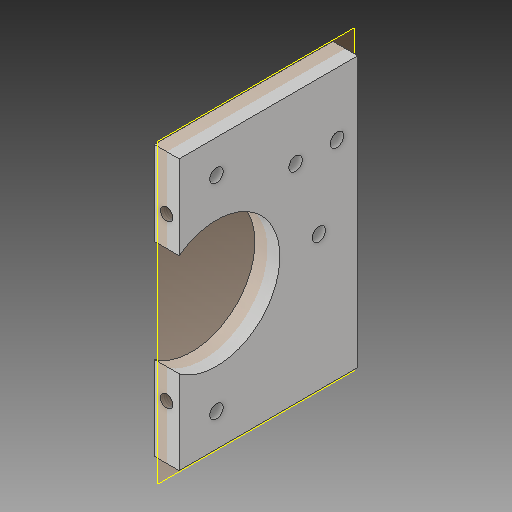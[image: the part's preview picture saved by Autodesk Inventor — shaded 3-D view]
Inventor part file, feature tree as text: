
AUTODESK INVENTOR PART (.ipt)
format: ipt  version: 2018 (Build 220112000, 112)  size: 161,792 bytes
history: native  units: mm
features: extrude x5, sketch x5, thread x4, reference x2, plane x1
ambient origin geometry x8: Origin, YZ Plane, XZ Plane, XY Plane, X Axis, Y Axis, Z Axis, Center Point
bodies: Solid1 (feature_tree)
feature tree (17):
  extrude  "Extrusion1"  Depth=86.0mm
  extrude  "Extrusion2"  Depth=12.0mm
  plane  "Work Plane1"
  extrude  "Extrusion3"  Depth=98.429mm
  extrude  "Extrusion4"  Depth=6.5mm
  extrude  "Extrusion6"  Depth=10.0mm
  thread  "Thread1"  [1 undecoded]
  thread  "Thread2"  [1 undecoded]
  thread  "Thread3"  [1 undecoded]
  thread  "Thread4"  [1 undecoded]
  sketch  "Sketch1"  dims[d0=130.0mm d1=86.0mm]
  sketch  "Sketch2"  dims[d2=12.0mm d3=0.0mm d4=18.0mm]
  sketch  "Sketch3"  dims[d5=18.0mm d6=98.429mm]
  sketch  "Sketch4"  dims[d7=6.5mm d8=6.5mm]
  sketch  "Sketch6"  dims[d9=6.5mm d10=49.2145mm d11=12.0mm d12=0.0mm d13=61.0mm d14=6.0mm d15=26.0mm d17=8.0mm d19=15.0mm d20=0.0mm d21=6.0mm d22=27.0mm d23=15.0mm d25=15.0mm d26=0.0mm d29=18.0mm d30=10.0mm d31=0.0mm d32=0.25mm d33=0.25mm d34=10.0mm d35=0.0mm d36=10.0mm d37=0.0mm d38=10.0mm d39=0.0mm d40=10.0mm d41=0.0mm]
  reference  "Reference3"
  reference  "Reference4"
note: 4 required parameter values undecoded (feature->parameter linkage not recoverable at this tier; creation-order binding heuristic only, values carry confidence <= 0.55)
